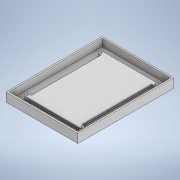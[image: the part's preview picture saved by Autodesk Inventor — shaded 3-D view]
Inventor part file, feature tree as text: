
AUTODESK INVENTOR PART (.ipt)
format: ipt  version: 2020.2 (Build 242310000, 310)  size: 535,040 bytes
history: native  units: in
note: dims shown in document units (in); Inventor stores cm internally (conversion verified against a paired STEP export)
features: sketch x11, extrude x6, other x5, hole x4, projected_geometry x3, shell x2, move_body x1, fillet x1, plane x1, chamfer x1
ambient origin geometry x8: Origin, YZ Plane, XZ Plane, XY Plane, X Axis, Y Axis, Z Axis, Center Point
bodies: Body1 (feature_tree), Body2 (feature_tree), Body3 (feature_tree)
feature tree (35):
  other  "Inner Case"
  extrude  "Extrusion1"  Depth=8.0525in
  shell  "Shell1"  Thickness=0.75in
  extrude  "Extrusion2"  Depth=4.217in
  move_body  "Move Body1"
  extrude  "Extrusion3"  Depth=6.5in
  extrude  "Extrusion4"  Depth=0.6515in
  extrude  "Extrusion5"  Depth=0.322in
  fillet  "Fillet1"  Radius=0.322in
  hole  "Hole1"  [1 undecoded]
  hole  "Hole2"  [1 undecoded]
  hole  "Hole3"  [1 undecoded]
  hole  "Hole4"  [1 undecoded]
  plane  "Work Plane1"
  extrude  "Extrusion7"  Depth=6.4375in
  chamfer  "Chamfer2"  Distance=0.031in
  shell  "Shell3"  Thickness=0.258in
  other  "Grill3"
  other  "Grill4"
  sketch  "Sketch1"  dims[d0=6.0213in d1=8.0525in d2=0.75in d3=0.0in]
  sketch  "Sketch2"  dims[d4=0.125in d5=4.217in]
  other  "Dispaly"
  sketch  "Sketch3"  dims[d6=6.5in d7=0.777in]
  sketch  "Sketch5"  dims[d8=0.6515in d9=0.335in]
  sketch  "Sketch6"  dims[d10=0.322in d11=0.335in d12=0.322in d13=0.335in d14=0.322in]
  sketch  "Sketch7"  dims[d15=0.335in d16=0.322in d17=0.161in]
  sketch  "Sketch8"  dims[d18=0.115in d19=0.115in]
  sketch  "Sketch9"  dims[d20=0.115in d21=0.115in]
  sketch  "Sketch14"  dims[d22=0.065in d23=0.0in d24=0.1217in d25=0.258in d26=0.0in]
  projected_geometry  "Projected Loop4"
  other  "Vented Case"
  sketch  "Sketch15"  dims[d27=3.943in d28=6.4375in]
  projected_geometry  "Projected Loop5"
  sketch  "Sketch16"  dims[d29=0.137in d30=0.031in d31=0.258in d32=0.0in d34=1.0in d35=0.0in d36=0.1in d37=0.1in d38=0.1in d39=0.1in d40=0.133in d41=0.0in d42=0.0625in d43=0.0968in d44=0.125in d45=0.375in d46=0.25in d47=0.5635in d48=0.125in d49=0.0in d50=0.0968in d51=0.125in d52=0.375in d53=0.25in d54=0.5635in d55=0.125in d56=0.0in d57=0.0968in d58=0.125in d59=0.375in d60=0.25in d61=0.5635in d62=0.125in d63=0.0in d64=0.0968in d65=0.125in d66=0.375in d67=0.25in d68=0.5635in d69=0.125in d70=0.0in d71=1.5625in d134=0.15in d135=1.6in d136=0.0in d137=0.5in d138=0.125in d139=45.0deg d140=0.125in d141=0.1in d142=0.1289in d143=11.0236in d145=0.2578in d146=0.3937in d148=1.0in d150=0.1in d151=0.125in d152=0.0in d153=0.0in d154=0.125in d155=0.0in d156=0.1in d157=0.0in d158=0.0in d159=0.05in d160=0.0in d161=0.0in d162=0.0in d163=5.7305in d164=0.1in d165=0.1289in d166=11.0236in d168=0.2578in d169=0.3937in d171=1.0in d173=0.1in d174=0.125in d175=0.0in d176=0.0in d177=0.125in d178=0.0in d179=0.1in d180=0.0in d181=0.0in d182=0.05in d183=0.0in d184=0.0in d185=0.0in d186=5.6919in d187=3.983in d188=6.5775in d189=0.7725in d190=0.638in]
  projected_geometry  "Projected Loop6"
note: 4 required parameter values undecoded (feature->parameter linkage not recoverable at this tier; creation-order binding heuristic only, values carry confidence <= 0.55)
